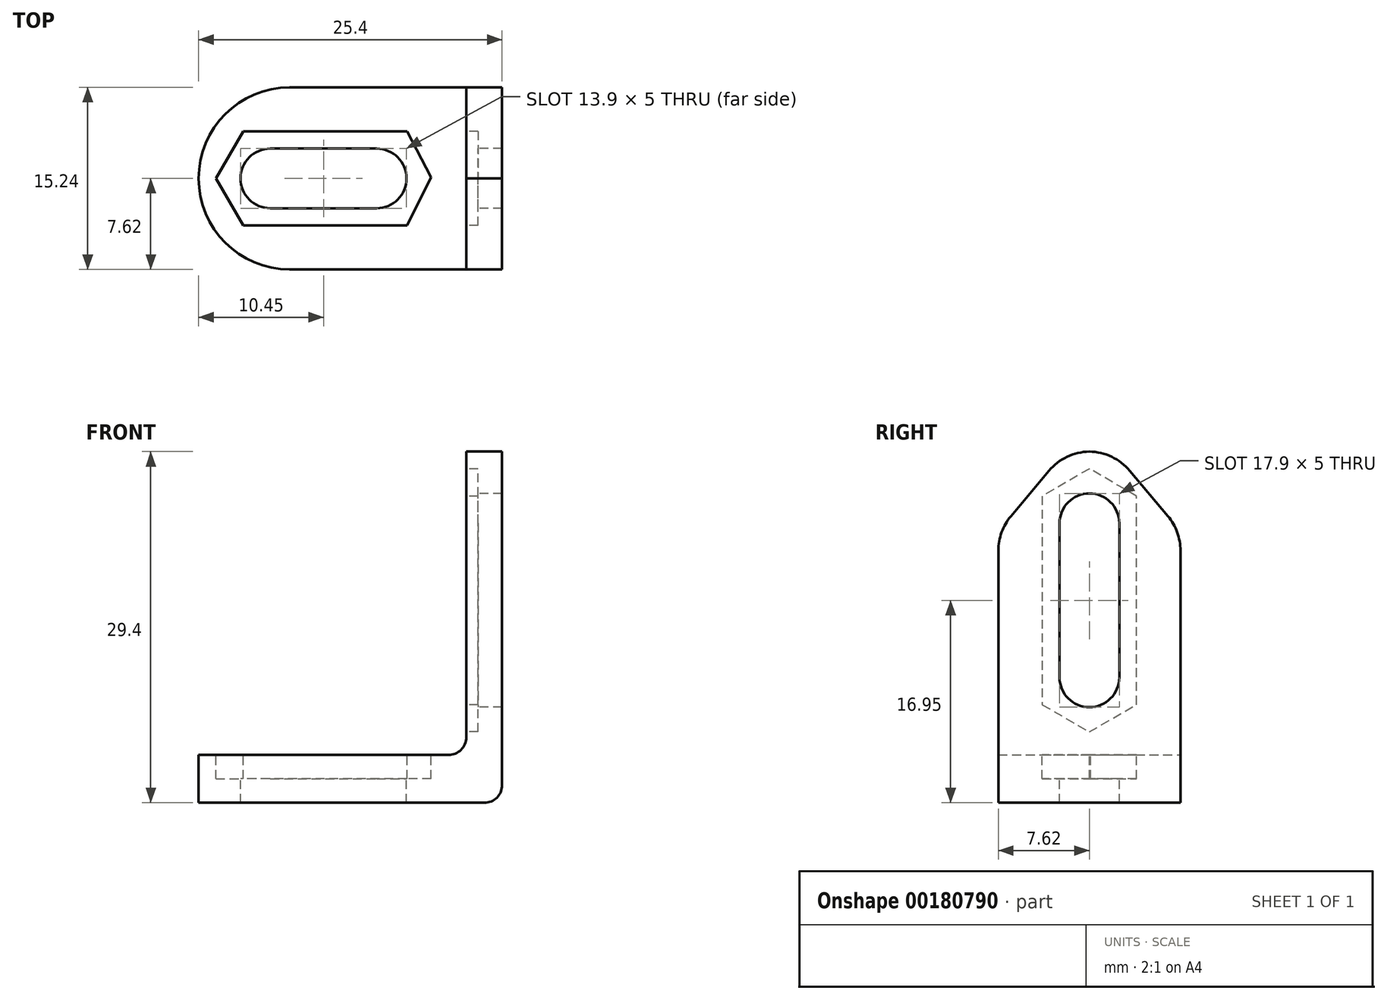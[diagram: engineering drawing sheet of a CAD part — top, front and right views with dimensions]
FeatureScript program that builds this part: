
annotation { "Feature Type Name" : "Feature", "Feature Type Description" : "" }
export const myFeature = defineFeature(function(context is Context, id is Id, definition is map)
    precondition{}
    {
        {
            var Q0;
            Q0=qCreatedBy(makeId("Front.planeOp"),FACE);
            var sketch = newSketch(context, id + "F0", { "sketchPlane" : qUnion([Q0])});
            skLineSegment(sketch, "E0.top", {"start": v(-4.5, 3) * mm, "end": v(-25.4, 3) * mm});
            skLineSegment(sketch, "E1.top", {"start": v(-1.5, 28.4) * mm, "end": v(-1.5, 28.4) * mm});
            skLineSegment(sketch, "E1.left", {"start": v(0, 0.5) * mm, "end": v(0, 28.4) * mm});
            skLineSegment(sketch, "E1.right", {"start": v(-3, 4.5) * mm, "end": v(-3, 28.4) * mm});
            skPoint(sketch, "E2.visualSharp", {"position": v(-3, 3) * mm});
            skArc(sketch, "E2.filletArc", {"start": v(-4.5, 3) * mm, "mid": v(-3.44, 3.44) * mm, "end": v(-3, 4.5) * mm});
            skPoint(sketch, "E3.visualSharp", {"position": v(0, 0) * mm});
            skPoint(sketch, "E4.visualSharp", {"position": v(-3, 28.4) * mm});
            skPoint(sketch, "E5.visualSharp", {"position": v(0, 28.4) * mm});
            skPoint(sketch, "E6.visualSharp", {"position": v(-52.3, 3) * mm});
            skLineSegment(sketch, "E7", {"start": v(-25.4, -1) * mm, "end": v(-1.5, -1) * mm});
            skPoint(sketch, "E8.visualSharp", {"position": v(-52.3, -1) * mm});
            skPoint(sketch, "E9.visualSharp", {"position": v(0, -1) * mm});
            skArc(sketch, "E9.filletArc", {"start": v(-1.5, -1) * mm, "mid": v(-0.44, -0.56) * mm, "end": v(0, 0.5) * mm});
            skLineSegment(sketch, "E10", {"start": v(-3, 28.4) * mm, "end": v(0, 28.4) * mm});
            skLineSegment(sketch, "E11.trimOffspring", {"start": v(-25.4, 3) * mm, "end": v(-25.4, -1) * mm});
            skSolve(sketch);
        }
        {
            var Q0;
            Q0=qSketchRegion(id+"F0",true);
            extrude(context, id + "F1", {"entities" : qUnion([Q0]), "depth" : 15.24 * mm});
        }
        {
            var Q0;
            Q0=makeQuery(id+"F1.opExtrude","SWEPT_FACE",FACE,{"disambiguationData":[OSD([sQuery(id+"F0.wireOp",EDGE,"E1.right")])]});
            var sketch = newSketch(context, id + "F2", { "sketchPlane" : qUnion([Q0])});
            skLineSegment(sketch, "E12", {"start": v(7.62, 22.4) * mm, "end": v(7.62, 9.5) * mm});
            skArc(sketch, "E13.0.startCap", {"start": v(5.12, 22.4) * mm, "mid": v(7.62, 24.9) * mm, "end": v(10.12, 22.4) * mm});
            skArc(sketch, "E13.0.endCap", {"start": v(10.12, 9.5) * mm, "mid": v(7.62, 7) * mm, "end": v(5.12, 9.5) * mm});
            skLineSegment(sketch, "E13.0.left", {"start": v(10.12, 22.4) * mm, "end": v(10.12, 9.5) * mm});
            skLineSegment(sketch, "E13.0.right", {"start": v(5.12, 22.4) * mm, "end": v(5.12, 9.5) * mm});
            skLineSegment(sketch, "E14.0.left", {"start": v(11.57, 22.4) * mm, "end": v(11.57, 9.5) * mm});
            skLineSegment(sketch, "E14.0.right", {"start": v(3.67, 22.4) * mm, "end": v(3.67, 9.5) * mm});
            skArc(sketch, "E15.cCircle", {"start": v(3.67, 22.4) * mm, "mid": v(7.62, 18.45) * mm, "end": v(11.57, 22.4) * mm, "construction": true});
            skLineSegment(sketch, "E15.0", {"start": v(11.57, 24.68) * mm, "end": v(11.57, 20.12) * mm});
            skLineSegment(sketch, "E15.3", {"start": v(3.67, 20.12) * mm, "end": v(3.67, 24.68) * mm});
            skLineSegment(sketch, "E15.4", {"start": v(3.67, 24.68) * mm, "end": v(7.62, 26.96) * mm});
            skLineSegment(sketch, "E15.5", {"start": v(7.62, 26.96) * mm, "end": v(11.57, 24.68) * mm});
            skPoint(sketch, "E15.0.midPoint", {"position": v(11.57, 22.4) * mm});
            skArc(sketch, "E16.cCircle", {"start": v(11.57, 9.5) * mm, "mid": v(7.62, 13.45) * mm, "end": v(3.67, 9.5) * mm, "construction": true});
            skLineSegment(sketch, "E16.0", {"start": v(11.57, 11.78) * mm, "end": v(11.57, 7.22) * mm});
            skLineSegment(sketch, "E16.1", {"start": v(11.57, 7.22) * mm, "end": v(7.62, 4.94) * mm});
            skLineSegment(sketch, "E16.2", {"start": v(7.62, 4.94) * mm, "end": v(3.67, 7.22) * mm});
            skLineSegment(sketch, "E16.3", {"start": v(3.67, 7.22) * mm, "end": v(3.67, 11.78) * mm});
            skPoint(sketch, "E16.0.midPoint", {"position": v(11.57, 9.5) * mm});
            skPoint(sketch, "E17.orphan", {"position": v(7.62, 14.06) * mm});
            skSolve(sketch);
        }
        {
            var Q0;
            Q0=qSketchRegion(id+"F2",true);
            extrude(context, id + "F3", {"entities" : qUnion([Q0]), "operationType" : NewBodyOperationType.REMOVE, "oppositeDirection" : true, "depth" : 1 * mm});
        }
        {
            var Q0;
            Q0=makeQuery(id+"F3.boolean.opBoolean","SPLIT",FACE,{"disambiguationData":[TD([makeQuery(id+"F3.opExtrude","SWEPT_FACE",FACE,{"disambiguationData":[OSD([sQuery(id+"F2.wireOp",EDGE,"E13.0.startCap")])]})])],"derivedFrom":makeQuery(id+"F1.opExtrude","SWEPT_FACE",FACE,{"disambiguationData":[OSD([sQuery(id+"F0.wireOp",EDGE,"E1.right")])]})});
            extrude(context, id + "F4", {"entities" : qUnion([Q0]), "operationType" : NewBodyOperationType.REMOVE, "endBound" : BoundingType.UP_TO_NEXT, "oppositeDirection" : true, "depth" : 25.4 * mm});
        }
        {
            var Q0;
            Q0=makeQuery(id+"F1.opExtrude","SWEPT_FACE",FACE,{"disambiguationData":[OSD([sQuery(id+"F0.wireOp",EDGE,"E0.top")])]});
            var sketch = newSketch(context, id + "F5", { "sketchPlane" : qUnion([Q0])});
            skLineSegment(sketch, "E18", {"start": v(-19.4, -7.62) * mm, "end": v(-10.5, -7.62) * mm});
            skPoint(sketch, "E18.startSnap0", {"position": v(-4.5, -7.62) * mm});
            skPoint(sketch, "E18.endSnap0", {"position": v(-4.5, -7.62) * mm});
            skArc(sketch, "E19.0.startCap", {"start": v(-19.4, -10.12) * mm, "mid": v(-21.9, -7.62) * mm, "end": v(-19.4, -5.12) * mm});
            skArc(sketch, "E19.0.endCap", {"start": v(-10.5, -5.12) * mm, "mid": v(-8, -7.62) * mm, "end": v(-10.5, -10.12) * mm});
            skLineSegment(sketch, "E19.0.left", {"start": v(-19.4, -5.12) * mm, "end": v(-10.5, -5.12) * mm});
            skLineSegment(sketch, "E19.0.right", {"start": v(-19.4, -10.12) * mm, "end": v(-10.5, -10.12) * mm});
            skArc(sketch, "E20.cCircle", {"start": v(-19.4, -11.57) * mm, "mid": v(-15.45, -7.62) * mm, "end": v(-19.4, -3.67) * mm, "construction": true});
            skLineSegment(sketch, "E20.0", {"start": v(-7.96, -11.57) * mm, "end": v(-21.68, -11.57) * mm});
            skLineSegment(sketch, "E20.1", {"start": v(-21.68, -11.57) * mm, "end": v(-23.96, -7.62) * mm});
            skLineSegment(sketch, "E20.2", {"start": v(-23.96, -7.62) * mm, "end": v(-21.68, -3.67) * mm});
            skLineSegment(sketch, "E20.3", {"start": v(-21.68, -3.67) * mm, "end": v(-7.96, -3.67) * mm});
            skPoint(sketch, "E20.0.midPoint", {"position": v(-19.4, -11.57) * mm});
            skLineSegment(sketch, "E21.4", {"start": v(-7.96, -3.67) * mm, "end": v(-5.94, -7.52) * mm});
            skLineSegment(sketch, "E21.5", {"start": v(-5.94, -7.52) * mm, "end": v(-7.96, -11.57) * mm});
            skPoint(sketch, "E22.orphan", {"position": v(-14.84, -7.62) * mm});
            skSolve(sketch);
        }
        {
            var Q0;
            Q0=qSketchRegion(id+"F5",true);
            extrude(context, id + "F6", {"entities" : qUnion([Q0]), "operationType" : NewBodyOperationType.REMOVE, "oppositeDirection" : true, "depth" : 2 * mm});
        }
        {
            var Q0;
            Q0=makeQuery(id+"F6.boolean.opBoolean","SPLIT",FACE,{"disambiguationData":[TD([makeQuery(id+"F6.opExtrude","SWEPT_FACE",FACE,{"disambiguationData":[OSD([sQuery(id+"F5.wireOp",EDGE,"E19.0.startCap")])]})])],"derivedFrom":makeQuery(id+"F1.opExtrude","SWEPT_FACE",FACE,{"disambiguationData":[OSD([sQuery(id+"F0.wireOp",EDGE,"E0.top")])]})});
            extrude(context, id + "F7", {"entities" : qUnion([Q0]), "operationType" : NewBodyOperationType.REMOVE, "endBound" : BoundingType.UP_TO_NEXT, "oppositeDirection" : true, "depth" : 25.4 * mm});
        }
        {
            var Q0;
            Q0=makeQuery(id+"F1.opExtrude","CAP_EDGE",EDGE,{"disambiguationData":[OSD([sQuery(id+"F0.wireOp",EDGE,"E10")])],"isStart":false});
            var Q1;
            Q1=makeQuery(id+"F1.opExtrude","CAP_EDGE",EDGE,{"disambiguationData":[OSD([sQuery(id+"F0.wireOp",EDGE,"E10")])],"isStart":true});
            chamfer(context, id + "F8", {"entities" : qUnion([Q0, Q1]), "chamferType" : ChamferType.OFFSET_ANGLE, "width" : 5.6 * mm, "oppositeDirection" : false, "angle" : 50 * degree, "tangentPropagation" : true});
        }
        {
            var Q0;
            {var subQ0=sQuery(id+"F0.wireOp",EDGE,"E10");Q0=makeQuery(id+"F8.opChamfer","BLEND_EDGE",EDGE,{"blendedFrom":[makeQuery(id+"F1.opExtrude","CAP_EDGE",EDGE,{"disambiguationData":[OSD([subQ0])],"isStart":false}),makeQuery(id+"F1.opExtrude","CAP_FACE",FACE,{"disambiguationData":[OSD([sQuery(id+"F0.wireOp",EDGE,"E0.top"),sQuery(id+"F0.wireOp",EDGE,"E1.left"),sQuery(id+"F0.wireOp",EDGE,"E1.right"),sQuery(id+"F0.wireOp",EDGE,"E2.filletArc"),sQuery(id+"F0.wireOp",EDGE,"E7"),sQuery(id+"F0.wireOp",EDGE,"E9.filletArc"),subQ0,sQuery(id+"F0.wireOp",EDGE,"E11.trimOffspring")])],"isStart":false})],"blendedInto":[makeQuery(id+"F1.opExtrude","CAP_FACE",FACE,{"disambiguationData":[OSD([sQuery(id+"F0.wireOp",EDGE,"E0.top"),sQuery(id+"F0.wireOp",EDGE,"E1.left"),sQuery(id+"F0.wireOp",EDGE,"E1.right"),sQuery(id+"F0.wireOp",EDGE,"E2.filletArc"),sQuery(id+"F0.wireOp",EDGE,"E7"),sQuery(id+"F0.wireOp",EDGE,"E9.filletArc"),subQ0,sQuery(id+"F0.wireOp",EDGE,"E11.trimOffspring")])],"isStart":false})]});}
            var Q1;
            {var subQ0=sQuery(id+"F0.wireOp",EDGE,"E10");Q1=makeQuery(id+"F8.opChamfer","BLEND_EDGE",EDGE,{"blendedFrom":[makeQuery(id+"F1.opExtrude","CAP_EDGE",EDGE,{"disambiguationData":[OSD([subQ0])],"isStart":false}),makeQuery(id+"F1.opExtrude","SWEPT_FACE",FACE,{"disambiguationData":[OSD([subQ0])]})],"blendedInto":[makeQuery(id+"F1.opExtrude","SWEPT_FACE",FACE,{"disambiguationData":[OSD([subQ0])]})]});}
            var Q2;
            {var subQ0=sQuery(id+"F0.wireOp",EDGE,"E10");Q2=makeQuery(id+"F8.opChamfer","BLEND_EDGE",EDGE,{"blendedFrom":[makeQuery(id+"F1.opExtrude","CAP_EDGE",EDGE,{"disambiguationData":[OSD([subQ0])],"isStart":true}),makeQuery(id+"F1.opExtrude","SWEPT_FACE",FACE,{"disambiguationData":[OSD([subQ0])]})],"blendedInto":[makeQuery(id+"F1.opExtrude","SWEPT_FACE",FACE,{"disambiguationData":[OSD([subQ0])]})]});}
            var Q3;
            {var subQ0=sQuery(id+"F0.wireOp",EDGE,"E10");Q3=makeQuery(id+"F8.opChamfer","BLEND_EDGE",EDGE,{"blendedFrom":[makeQuery(id+"F1.opExtrude","CAP_EDGE",EDGE,{"disambiguationData":[OSD([subQ0])],"isStart":true}),makeQuery(id+"F1.opExtrude","CAP_FACE",FACE,{"disambiguationData":[OSD([sQuery(id+"F0.wireOp",EDGE,"E0.top"),sQuery(id+"F0.wireOp",EDGE,"E1.left"),sQuery(id+"F0.wireOp",EDGE,"E1.right"),sQuery(id+"F0.wireOp",EDGE,"E2.filletArc"),sQuery(id+"F0.wireOp",EDGE,"E7"),sQuery(id+"F0.wireOp",EDGE,"E9.filletArc"),subQ0,sQuery(id+"F0.wireOp",EDGE,"E11.trimOffspring")])],"isStart":true})],"blendedInto":[makeQuery(id+"F1.opExtrude","CAP_FACE",FACE,{"disambiguationData":[OSD([sQuery(id+"F0.wireOp",EDGE,"E0.top"),sQuery(id+"F0.wireOp",EDGE,"E1.left"),sQuery(id+"F0.wireOp",EDGE,"E1.right"),sQuery(id+"F0.wireOp",EDGE,"E2.filletArc"),sQuery(id+"F0.wireOp",EDGE,"E7"),sQuery(id+"F0.wireOp",EDGE,"E9.filletArc"),subQ0,sQuery(id+"F0.wireOp",EDGE,"E11.trimOffspring")])],"isStart":true})]});}
            fillet(context, id + "F9", {"entities" : qUnion([Q0, Q1, Q2, Q3]), "radius" : 4.5 * mm, "tangentPropagation" : true, "allowEdgeOverflow" : false});
        }
        {
            var Q0;
            Q0=makeQuery(id+"F1.opExtrude","CAP_EDGE",EDGE,{"disambiguationData":[OSD([sQuery(id+"F0.wireOp",EDGE,"E11.trimOffspring")])],"isStart":false});
            var Q1;
            Q1=makeQuery(id+"F1.opExtrude","CAP_EDGE",EDGE,{"disambiguationData":[OSD([sQuery(id+"F0.wireOp",EDGE,"E11.trimOffspring")])],"isStart":true});
            fillet(context, id + "F10", {"entities" : qUnion([Q0, Q1]), "radius" : 7.62 * mm, "tangentPropagation" : true, "allowEdgeOverflow" : false});
        }
    });
